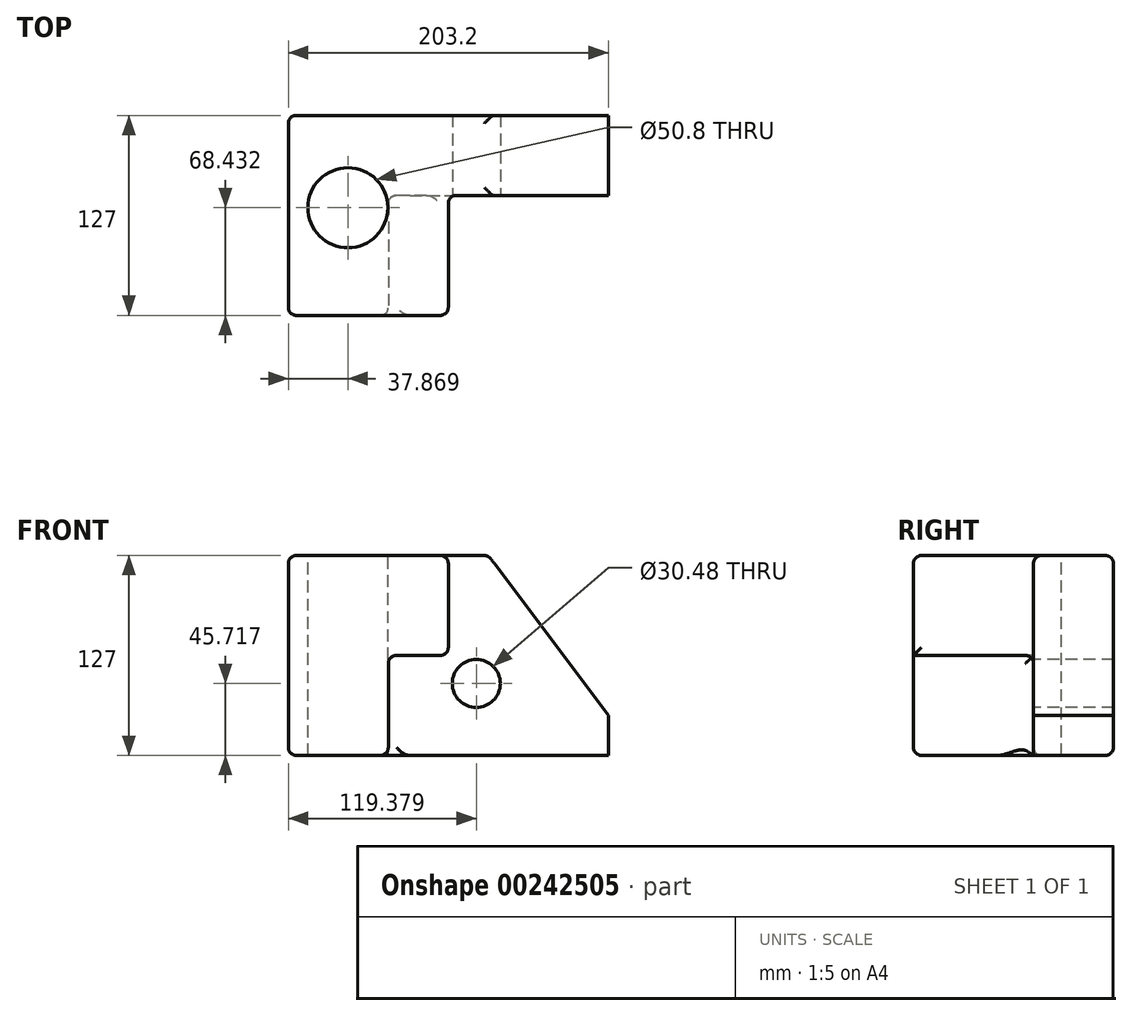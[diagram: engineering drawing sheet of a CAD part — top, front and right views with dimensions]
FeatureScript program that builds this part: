
annotation { "Feature Type Name" : "Feature", "Feature Type Description" : "" }
export const myFeature = defineFeature(function(context is Context, id is Id, definition is map)
    precondition{}
    {
        {
            var Q0;
            Q0=qCreatedBy(makeId("Front.planeOp"),FACE);
            var sketch = newSketch(context, id + "F0", { "sketchPlane" : qUnion([Q0])});
            skLineSegment(sketch, "E0.bottom", {"start": v(-100.95, 61.68) * mm, "end": v(102.25, 61.68) * mm});
            skLineSegment(sketch, "E0.top", {"start": v(-100.95, -65.32) * mm, "end": v(102.25, -65.32) * mm});
            skLineSegment(sketch, "E0.left", {"start": v(-100.95, 61.68) * mm, "end": v(-100.95, -65.32) * mm});
            skLineSegment(sketch, "E0.right", {"start": v(102.25, 61.68) * mm, "end": v(102.25, -65.32) * mm});
            skSolve(sketch);
        }
        {
            var Q0;
            Q0 = qSketchRegion(id + "F0", true);
            extrude(context, id + "F1", {"entities" : qUnion([Q0]), "depth" : 127 * mm});
        }
        {
            var Q0;
            Q0=makeQuery(id+"F1.opExtrude","CAP_FACE",FACE,{"disambiguationData":[OSD([sQuery(id+"F0.wireOp",EDGE,"E0.bottom"),sQuery(id+"F0.wireOp",EDGE,"E0.top"),sQuery(id+"F0.wireOp",EDGE,"E0.left"),sQuery(id+"F0.wireOp",EDGE,"E0.right")])],"isStart":false});
            var sketch = newSketch(context, id + "F2", { "sketchPlane" : qUnion([Q0])});
            skLineSegment(sketch, "E1", {"start": v(-100.95, 61.68) * mm, "end": v(0.65, 61.68) * mm});
            skLineSegment(sketch, "E2", {"start": v(0.65, 61.68) * mm, "end": v(0.65, -1.82) * mm});
            skLineSegment(sketch, "E3", {"start": v(0.65, -1.82) * mm, "end": v(-37.45, -1.82) * mm});
            skLineSegment(sketch, "E4", {"start": v(-37.45, -1.82) * mm, "end": v(-37.45, -65.32) * mm});
            skLineSegment(sketch, "E5", {"start": v(-37.45, -65.32) * mm, "end": v(-100.95, -65.32) * mm});
            skLineSegment(sketch, "E6", {"start": v(-100.95, -65.32) * mm, "end": v(-100.95, 61.68) * mm});
            skSolve(sketch);
        }
        {
            var Q0;
            {var subQ2=sQuery(id+"F2.wireOp",EDGE,"E2");Q0=makeQuery(id+"F2.imprint","IMPRINT",FACE,{"disambiguationData":[TD([[makeQuery(id+"F2.imprint","IMPRINT",EDGE,{"derivedFrom":subQ2}),1.0]])]});}
            extrude(context, id + "F3", {"entities" : qUnion([Q0]), "operationType" : NewBodyOperationType.REMOVE, "oppositeDirection" : true, "depth" : 76.2 * mm});
        }
        {
            var Q0;
            Q0=makeQuery(id+"F1.opExtrude","SWEPT_EDGE",EDGE,{"disambiguationData":[OSD([sQuery(id+"F0.wireOp",EDGE,"E0.bottom"),sQuery(id+"F0.wireOp",EDGE,"E0.right")])]});
            chamfer(context, id + "F4", {"entities" : qUnion([Q0]), "chamferType" : ChamferType.TWO_OFFSETS, "width1" : 76.2 * mm, "oppositeDirection" : false, "width2" : 101.6 * mm, "tangentPropagation" : true});
        }
        {
            var Q0;
            Q0=makeQuery(id+"F1.opExtrude","CAP_EDGE",EDGE,{"disambiguationData":[OSD([sQuery(id+"F0.wireOp",EDGE,"E0.bottom")])],"isStart":false});
            var Q1;
            Q1=makeQuery(id+"F1.opExtrude","SWEPT_FACE",FACE,{"disambiguationData":[OSD([sQuery(id+"F0.wireOp",EDGE,"E0.bottom")])]});
            var Q2;
            Q2=makeQuery(id+"F3.boolean.opBoolean","COPY",EDGE,{"derivedFrom":makeQuery(id+"F3.opExtrude","CAP_EDGE",EDGE,{"disambiguationData":[OSD([sQuery(id+"F2.wireOp",EDGE,"E2")])],"isStart":true})});
            var Q3;
            Q3=makeQuery(id+"F3.boolean.opBoolean","COPY",FACE,{"derivedFrom":makeQuery(id+"F3.opExtrude","SWEPT_FACE",FACE,{"disambiguationData":[OSD([sQuery(id+"F2.wireOp",EDGE,"E2")])]})});
            var Q4;
            Q4=makeQuery(id+"F3.boolean.opBoolean","COPY",FACE,{"derivedFrom":makeQuery(id+"F3.opExtrude","SWEPT_FACE",FACE,{"disambiguationData":[OSD([sQuery(id+"F2.wireOp",EDGE,"E4")])]})});
            var Q5;
            Q5=makeQuery(id+"F1.opExtrude","CAP_EDGE",EDGE,{"disambiguationData":[OSD([sQuery(id+"F0.wireOp",EDGE,"E0.top")])],"isStart":false});
            var Q6;
            Q6=makeQuery(id+"F1.opExtrude","SWEPT_FACE",FACE,{"disambiguationData":[OSD([sQuery(id+"F0.wireOp",EDGE,"E0.left")])]});
            var Q7;
            Q7=makeQuery(id+"F1.opExtrude","CAP_EDGE",EDGE,{"disambiguationData":[OSD([sQuery(id+"F0.wireOp",EDGE,"E0.top")])],"isStart":true});
            fillet(context, id + "F5", {"entities" : qUnion([Q0, Q1, Q2, Q3, Q4, Q5, Q6, Q7]), "radius" : 5.08 * mm, "tangentPropagation" : true, "allowEdgeOverflow" : false});
        }
        {
            var Q0;
            Q0=makeQuery(id+"F3.boolean.opBoolean","COPY",FACE,{"derivedFrom":makeQuery(id+"F3.opExtrude","CAP_FACE",FACE,{"disambiguationData":[OSD([sQuery(id+"F0.wireOp",EDGE,"E0.bottom"),sQuery(id+"F0.wireOp",EDGE,"E0.top"),sQuery(id+"F0.wireOp",EDGE,"E0.right"),sQuery(id+"F2.wireOp",EDGE,"E2"),sQuery(id+"F2.wireOp",EDGE,"E3"),sQuery(id+"F2.wireOp",EDGE,"E4")])],"isStart":false})});
            var sketch = newSketch(context, id + "F6", { "sketchPlane" : qUnion([Q0])});
            skCircle(sketch, "E7", {"center": v(18.43, -19.6) * mm, "radius": 15.24 * mm});
            skSolve(sketch);
        }
        {
            var Q0;
            Q0=makeQuery(id+"F6.imprint","IMPRINT",FACE,{"disambiguationData":[TD([[makeQuery(id+"F6.imprint","IMPRINT",EDGE,{"derivedFrom":sQuery(id+"F6.wireOp",EDGE,"E7")}),1.0]])]});
            var Q1;
            Q1=sQuery(id+"F6.wireOp",EDGE,"E7");
            var Q2;
            Q2=makeQuery(id+"F1.opExtrude","CAP_FACE",FACE,{"disambiguationData":[OSD([sQuery(id+"F0.wireOp",EDGE,"E0.bottom"),sQuery(id+"F0.wireOp",EDGE,"E0.top"),sQuery(id+"F0.wireOp",EDGE,"E0.left"),sQuery(id+"F0.wireOp",EDGE,"E0.right")])],"isStart":true});
            extrude(context, id + "F7", {"entities" : qUnion([Q0]), "operationType" : NewBodyOperationType.REMOVE, "surfaceEntities" : qUnion([Q1]), "endBound" : BoundingType.UP_TO_SURFACE, "oppositeDirection" : true, "endBoundEntityFace" : qUnion([Q2]), "depth" : 25.4 * mm});
        }
        {
            var Q0;
            Q0=makeQuery(id+"F1.opExtrude","SWEPT_FACE",FACE,{"disambiguationData":[OSD([sQuery(id+"F0.wireOp",EDGE,"E0.bottom")])]});
            var sketch = newSketch(context, id + "F8", { "sketchPlane" : qUnion([Q0])});
            skCircle(sketch, "E8", {"center": v(-63.08, -58.57) * mm, "radius": 25.4 * mm});
            skSolve(sketch);
        }
        {
            var Q0;
            Q0=makeQuery(id+"F8.imprint","IMPRINT",FACE,{"disambiguationData":[TD([[makeQuery(id+"F8.imprint","IMPRINT",EDGE,{"derivedFrom":sQuery(id+"F8.wireOp",EDGE,"E8")}),1.0]])]});
            extrude(context, id + "F9", {"entities" : qUnion([Q0]), "operationType" : NewBodyOperationType.REMOVE, "endBound" : BoundingType.UP_TO_NEXT, "oppositeDirection" : true, "depth" : 25.4 * mm});
        }
    });
